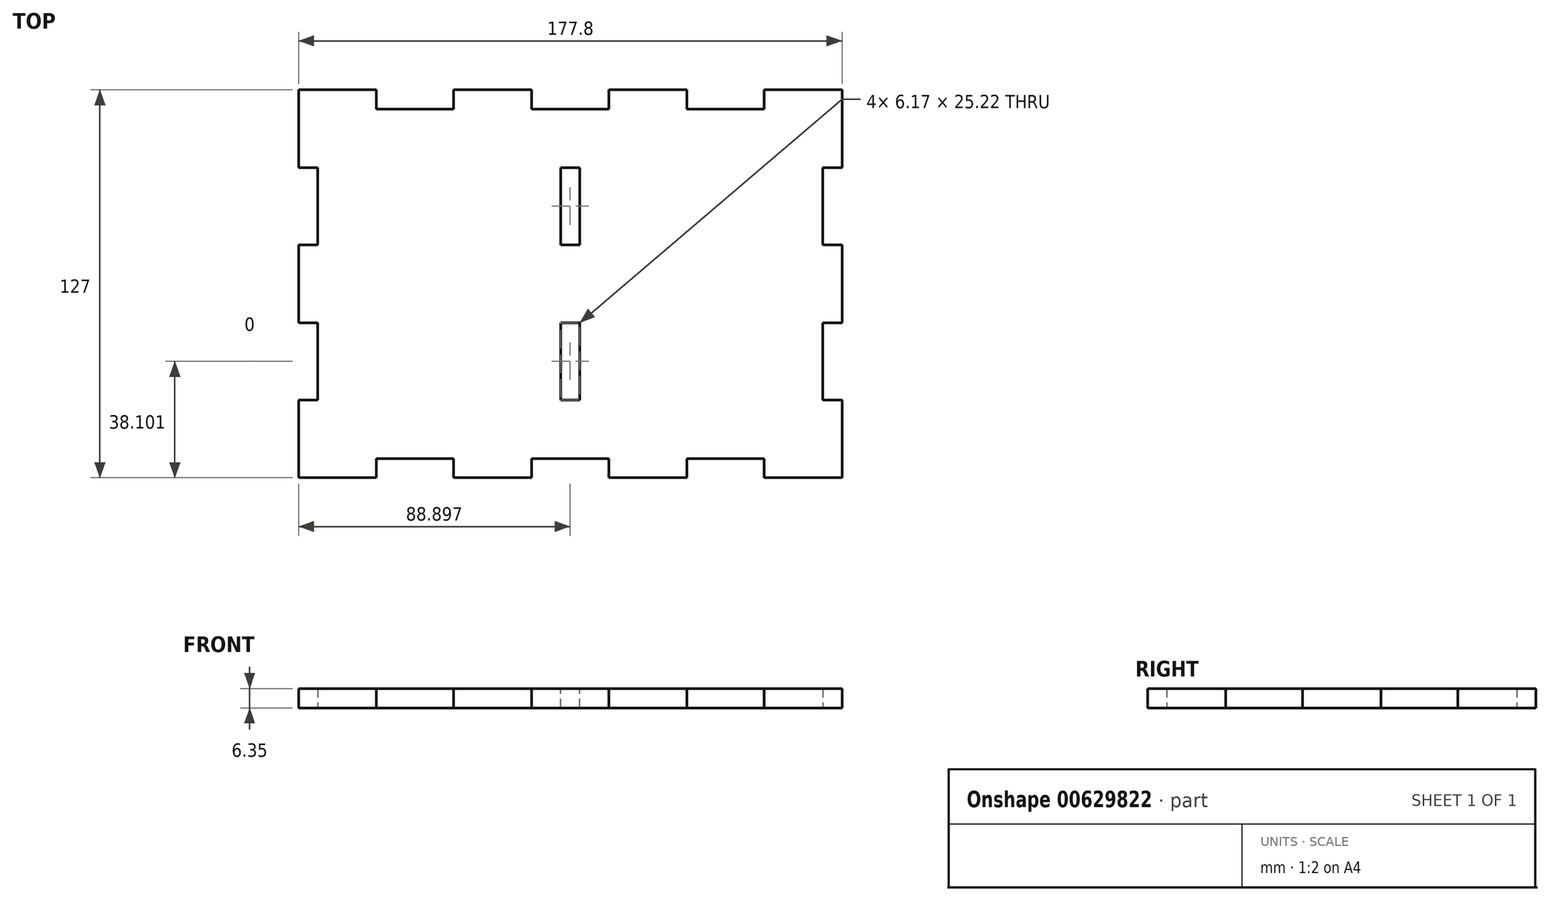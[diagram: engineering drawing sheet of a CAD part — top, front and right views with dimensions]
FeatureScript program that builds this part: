
annotation { "Feature Type Name" : "Feature", "Feature Type Description" : "" }
export const myFeature = defineFeature(function(context is Context, id is Id, definition is map)
    precondition{}
    {
        {
            var Q0;
            Q0=qCreatedBy(makeId("Top.planeOp"),FACE);
            var sketch = newSketch(context, id + "F0", { "sketchPlane" : qUnion([Q0])});
            skLineSegment(sketch, "E0.bottom", {"start": v(-53.03, 46.6) * mm, "end": v(-27.54, 46.6) * mm});
            skLineSegment(sketch, "E0.top", {"start": v(-53.03, -80.4) * mm, "end": v(-27.54, -80.4) * mm});
            skLineSegment(sketch, "E0.left", {"start": v(-53.03, 46.6) * mm, "end": v(-53.03, 21.11) * mm});
            skLineSegment(sketch, "E0.right", {"start": v(124.77, 46.6) * mm, "end": v(124.77, 21.11) * mm});
            skLineSegment(sketch, "E1.top", {"start": v(-27.54, -74.14) * mm, "end": v(-2.32, -74.14) * mm});
            skLineSegment(sketch, "E1.left", {"start": v(-27.54, -80.4) * mm, "end": v(-27.54, -74.14) * mm});
            skLineSegment(sketch, "E1.right", {"start": v(-2.32, -80.4) * mm, "end": v(-2.32, -74.14) * mm});
            skLineSegment(sketch, "E2.bottom", {"start": v(74.06, -74.14) * mm, "end": v(99.28, -74.14) * mm});
            skLineSegment(sketch, "E2.left", {"start": v(74.06, -74.14) * mm, "end": v(74.06, -80.4) * mm});
            skLineSegment(sketch, "E2.right", {"start": v(99.28, -74.14) * mm, "end": v(99.28, -80.4) * mm});
            skPoint(sketch, "E3", {"position": v(-14.93, -74.14) * mm});
            skPoint(sketch, "E4", {"position": v(86.67, -74.14) * mm});
            skLineSegment(sketch, "E5.bottom", {"start": v(23.26, -74.14) * mm, "end": v(48.48, -74.14) * mm});
            skLineSegment(sketch, "E5.left", {"start": v(23.26, -74.14) * mm, "end": v(23.26, -80.4) * mm});
            skLineSegment(sketch, "E5.right", {"start": v(48.48, -74.14) * mm, "end": v(48.48, -80.4) * mm});
            skPoint(sketch, "E6", {"position": v(35.87, -74.14) * mm});
            skLineSegment(sketch, "E7.bottom", {"start": v(118.5, -29.69) * mm, "end": v(124.77, -29.69) * mm});
            skLineSegment(sketch, "E7.top", {"start": v(118.5, -54.91) * mm, "end": v(124.77, -54.91) * mm});
            skLineSegment(sketch, "E7.left", {"start": v(118.5, -29.69) * mm, "end": v(118.5, -54.91) * mm});
            skPoint(sketch, "E8", {"position": v(118.5, -42.3) * mm});
            skLineSegment(sketch, "E9.bottom", {"start": v(124.77, 21.11) * mm, "end": v(118.5, 21.11) * mm});
            skLineSegment(sketch, "E9.top", {"start": v(124.77, -4.11) * mm, "end": v(118.5, -4.11) * mm});
            skLineSegment(sketch, "E9.right", {"start": v(118.5, 21.11) * mm, "end": v(118.5, -4.11) * mm});
            skPoint(sketch, "E10", {"position": v(118.5, 8.5) * mm});
            skPoint(sketch, "E11", {"position": v(124.77, -16.9) * mm});
            skPoint(sketch, "E12", {"position": v(-53.03, -16.9) * mm});
            skPoint(sketch, "E13", {"position": v(35.87, -80.4) * mm});
            skPoint(sketch, "E14", {"position": v(35.87, 46.6) * mm});
            skLineSegment(sketch, "E15", {"start": v(35.87, 40.34) * mm, "end": v(35.87, -74.14) * mm, "construction": true});
            skLineSegment(sketch, "E16.MirrorCS", {"start": v(124.77, -16.9) * mm, "end": v(-53.03, -16.9) * mm, "construction": true});
            skLineSegment(sketch, "E17.MirrorCS", {"start": v(-46.77, 21.11) * mm, "end": v(-46.77, -4.11) * mm});
            skLineSegment(sketch, "E18.MirrorCS", {"start": v(-53.03, -4.11) * mm, "end": v(-46.77, -4.11) * mm});
            skLineSegment(sketch, "E19.MirrorCS", {"start": v(-53.03, 21.11) * mm, "end": v(-46.77, 21.11) * mm});
            skLineSegment(sketch, "E20.MirrorCS", {"start": v(-46.77, -29.69) * mm, "end": v(-53.03, -29.69) * mm});
            skLineSegment(sketch, "E21.MirrorCS", {"start": v(-46.77, -29.69) * mm, "end": v(-46.77, -54.91) * mm});
            skLineSegment(sketch, "E22.MirrorCS", {"start": v(-46.77, -54.91) * mm, "end": v(-53.03, -54.91) * mm});
            skLineSegment(sketch, "E23.MirrorCS", {"start": v(-27.54, 46.6) * mm, "end": v(-27.54, 40.34) * mm});
            skLineSegment(sketch, "E24.MirrorCS", {"start": v(-27.54, 40.34) * mm, "end": v(-2.32, 40.34) * mm});
            skLineSegment(sketch, "E25.MirrorCS", {"start": v(-2.32, 46.6) * mm, "end": v(-2.32, 40.34) * mm});
            skLineSegment(sketch, "E26.MirrorCS", {"start": v(23.26, 40.34) * mm, "end": v(23.26, 46.6) * mm});
            skLineSegment(sketch, "E27.MirrorCS", {"start": v(23.26, 40.34) * mm, "end": v(48.48, 40.34) * mm});
            skLineSegment(sketch, "E28.MirrorCS", {"start": v(48.48, 40.34) * mm, "end": v(48.48, 46.6) * mm});
            skLineSegment(sketch, "E29.MirrorCS", {"start": v(74.06, 40.34) * mm, "end": v(74.06, 46.6) * mm});
            skLineSegment(sketch, "E30.MirrorCS", {"start": v(74.06, 40.34) * mm, "end": v(99.28, 40.34) * mm});
            skLineSegment(sketch, "E31.MirrorCS", {"start": v(99.28, 40.34) * mm, "end": v(99.28, 46.6) * mm});
            skLineSegment(sketch, "E32.trimOffspring", {"start": v(-53.03, -4.11) * mm, "end": v(-53.03, -29.69) * mm});
            skLineSegment(sketch, "E33.trimOffspring", {"start": v(-2.32, 46.6) * mm, "end": v(23.26, 46.6) * mm});
            skLineSegment(sketch, "E34.trimOffspring", {"start": v(-53.03, -54.91) * mm, "end": v(-53.03, -80.4) * mm});
            skLineSegment(sketch, "E35.trimOffspring", {"start": v(124.77, -54.91) * mm, "end": v(124.77, -80.4) * mm});
            skLineSegment(sketch, "E36.trimOffspring", {"start": v(124.77, -4.11) * mm, "end": v(124.77, -29.69) * mm});
            skLineSegment(sketch, "E37.trimOffspring", {"start": v(-2.32, -80.4) * mm, "end": v(23.26, -80.4) * mm});
            skLineSegment(sketch, "E38.trimOffspring", {"start": v(48.48, -80.4) * mm, "end": v(74.06, -80.4) * mm});
            skLineSegment(sketch, "E39.trimOffspring", {"start": v(99.28, -80.4) * mm, "end": v(124.77, -80.4) * mm});
            skLineSegment(sketch, "E40.trimOffspring", {"start": v(99.28, 46.6) * mm, "end": v(124.77, 46.6) * mm});
            skLineSegment(sketch, "E41.trimOffspring", {"start": v(48.48, 46.6) * mm, "end": v(74.06, 46.6) * mm});
            skSolve(sketch);
        }
        {
            var Q0;
            Q0=makeQuery(id+"F0.imprint","IMPRINT",FACE,{"disambiguationData":[TD([[makeQuery(id+"F0.imprint","IMPRINT",EDGE,{"derivedFrom":sQuery(id+"F0.wireOp",EDGE,"E0.bottom")}),-1.0]])]});
            extrude(context, id + "F1", {"entities" : qUnion([Q0]), "depth" : 6.35 * mm, "offsetDistance" : 25.4 * mm});
        }
        {
            var Q0;
            Q0=makeQuery(id+"F1.opExtrude","CAP_FACE",FACE,{"disambiguationData":[OSD([sQuery(id+"F0.wireOp",EDGE,"E0.bottom"),sQuery(id+"F0.wireOp",EDGE,"E0.top"),sQuery(id+"F0.wireOp",EDGE,"E0.left"),sQuery(id+"F0.wireOp",EDGE,"E0.right"),sQuery(id+"F0.wireOp",EDGE,"E1.top"),sQuery(id+"F0.wireOp",EDGE,"E1.left"),sQuery(id+"F0.wireOp",EDGE,"E1.right"),sQuery(id+"F0.wireOp",EDGE,"E2.bottom"),sQuery(id+"F0.wireOp",EDGE,"E2.left"),sQuery(id+"F0.wireOp",EDGE,"E2.right"),sQuery(id+"F0.wireOp",EDGE,"E5.bottom"),sQuery(id+"F0.wireOp",EDGE,"E5.left"),sQuery(id+"F0.wireOp",EDGE,"E5.right"),sQuery(id+"F0.wireOp",EDGE,"E7.bottom"),sQuery(id+"F0.wireOp",EDGE,"E7.top"),sQuery(id+"F0.wireOp",EDGE,"E7.left"),sQuery(id+"F0.wireOp",EDGE,"E9.bottom"),sQuery(id+"F0.wireOp",EDGE,"E9.top"),sQuery(id+"F0.wireOp",EDGE,"E9.right"),sQuery(id+"F0.wireOp",EDGE,"E17.MirrorCS"),sQuery(id+"F0.wireOp",EDGE,"E18.MirrorCS"),sQuery(id+"F0.wireOp",EDGE,"E19.MirrorCS"),sQuery(id+"F0.wireOp",EDGE,"E20.MirrorCS"),sQuery(id+"F0.wireOp",EDGE,"E21.MirrorCS"),sQuery(id+"F0.wireOp",EDGE,"E22.MirrorCS"),sQuery(id+"F0.wireOp",EDGE,"E23.MirrorCS"),sQuery(id+"F0.wireOp",EDGE,"E24.MirrorCS"),sQuery(id+"F0.wireOp",EDGE,"E25.MirrorCS"),sQuery(id+"F0.wireOp",EDGE,"E26.MirrorCS"),sQuery(id+"F0.wireOp",EDGE,"E27.MirrorCS"),sQuery(id+"F0.wireOp",EDGE,"E28.MirrorCS"),sQuery(id+"F0.wireOp",EDGE,"E29.MirrorCS"),sQuery(id+"F0.wireOp",EDGE,"E30.MirrorCS"),sQuery(id+"F0.wireOp",EDGE,"E31.MirrorCS"),sQuery(id+"F0.wireOp",EDGE,"E32.trimOffspring"),sQuery(id+"F0.wireOp",EDGE,"E33.trimOffspring"),sQuery(id+"F0.wireOp",EDGE,"E34.trimOffspring"),sQuery(id+"F0.wireOp",EDGE,"E35.trimOffspring"),sQuery(id+"F0.wireOp",EDGE,"E36.trimOffspring"),sQuery(id+"F0.wireOp",EDGE,"E37.trimOffspring"),sQuery(id+"F0.wireOp",EDGE,"E38.trimOffspring"),sQuery(id+"F0.wireOp",EDGE,"E39.trimOffspring"),sQuery(id+"F0.wireOp",EDGE,"E40.trimOffspring"),sQuery(id+"F0.wireOp",EDGE,"E41.trimOffspring")])],"isStart":false});
            var sketch = newSketch(context, id + "F2", { "sketchPlane" : qUnion([Q0])});
            skLineSegment(sketch, "E42.bottom", {"start": v(32.78, 21.11) * mm, "end": v(38.95, 21.11) * mm});
            skLineSegment(sketch, "E42.top", {"start": v(32.78, -4.11) * mm, "end": v(38.95, -4.11) * mm});
            skLineSegment(sketch, "E42.left", {"start": v(32.78, 21.11) * mm, "end": v(32.78, -4.11) * mm});
            skLineSegment(sketch, "E42.right", {"start": v(38.95, 21.11) * mm, "end": v(38.95, -4.11) * mm});
            skLineSegment(sketch, "E43.bottom", {"start": v(32.78, -29.69) * mm, "end": v(38.95, -29.69) * mm});
            skLineSegment(sketch, "E43.top", {"start": v(32.78, -54.91) * mm, "end": v(38.95, -54.91) * mm});
            skLineSegment(sketch, "E43.left", {"start": v(32.78, -29.69) * mm, "end": v(32.78, -54.91) * mm});
            skLineSegment(sketch, "E43.right", {"start": v(38.95, -29.69) * mm, "end": v(38.95, -54.91) * mm});
            skPoint(sketch, "E44", {"position": v(35.87, 21.11) * mm});
            skPoint(sketch, "E45", {"position": v(35.87, 40.34) * mm});
            skPoint(sketch, "E46", {"position": v(35.87, -29.69) * mm});
            skPoint(sketch, "E47", {"position": v(38.95, -42.3) * mm});
            skPoint(sketch, "E48", {"position": v(38.95, 8.5) * mm});
            skSolve(sketch);
        }
        {
            var Q0;
            Q0=makeQuery(id+"F2.imprint","IMPRINT",FACE,{"disambiguationData":[TD([[makeQuery(id+"F2.imprint","IMPRINT",EDGE,{"derivedFrom":sQuery(id+"F2.wireOp",EDGE,"E43.bottom")}),-1.0]])]});
            var Q1;
            Q1=makeQuery(id+"F2.imprint","IMPRINT",FACE,{"disambiguationData":[TD([[makeQuery(id+"F2.imprint","IMPRINT",EDGE,{"derivedFrom":sQuery(id+"F2.wireOp",EDGE,"E42.bottom")}),-1.0]])]});
            extrude(context, id + "F3", {"entities" : qUnion([Q0, Q1]), "operationType" : NewBodyOperationType.REMOVE, "oppositeDirection" : true, "depth" : 25.4 * mm, "offsetDistance" : 25.4 * mm});
        }
    });
